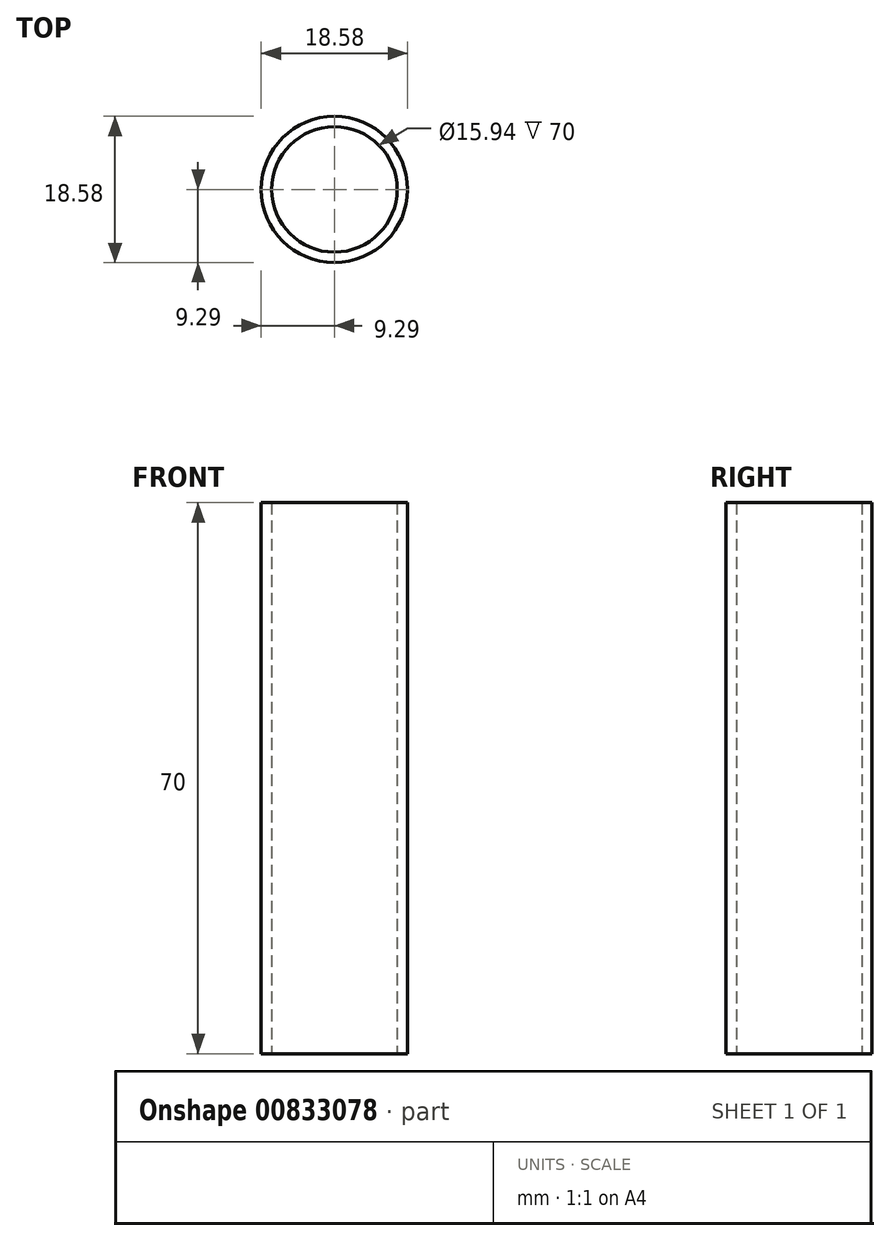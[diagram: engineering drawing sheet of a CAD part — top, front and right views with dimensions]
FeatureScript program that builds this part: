
annotation { "Feature Type Name" : "Feature", "Feature Type Description" : "" }
export const myFeature = defineFeature(function(context is Context, id is Id, definition is map)
    precondition{}
    {
        {
            var Q0;
            Q0=qCreatedBy(makeId("Top.planeOp"),FACE);
            var sketch = newSketch(context, id + "F0", { "sketchPlane" : qUnion([Q0])});
            skCircle(sketch, "E0", {"center": v(0, 0) * mm, "radius": 9.3 * mm});
            skCircle(sketch, "E1", {"center": v(0, 0) * mm, "radius": 7.97 * mm});
            skSolve(sketch);
        }
        {
            var Q0;
            Q0=makeQuery(id+"F0.imprint","IMPRINT",FACE,{"disambiguationData":[TD([[makeQuery(id+"F0.imprint","IMPRINT",EDGE,{"derivedFrom":sQuery(id+"F0.wireOp",EDGE,"E0")}),1.0]])]});
            extrude(context, id + "F1", {"entities" : qUnion([Q0]), "depth" : 70 * mm, "offsetDistance" : 25 * mm});
        }
        {
            var Q0;
            Q0=qCreatedBy(makeId("Right.planeOp"),FACE);
            var sketch = newSketch(context, id + "F2", { "sketchPlane" : qUnion([Q0])});
            skCircle(sketch, "E2", {"center": v(0, 60.33) * mm, "radius": 5.53 * mm});
            skSolve(sketch);
        }
        {
            var Q0;
            Q0=sQuery(id+"F2.wireOp",EDGE,"E2");
            extrude(context, id + "F3", {"bodyType" : ToolBodyType.SURFACE, "surfaceEntities" : qUnion([Q0]), "depth" : 60 * mm, "offsetDistance" : 25 * mm});
        }
    });
